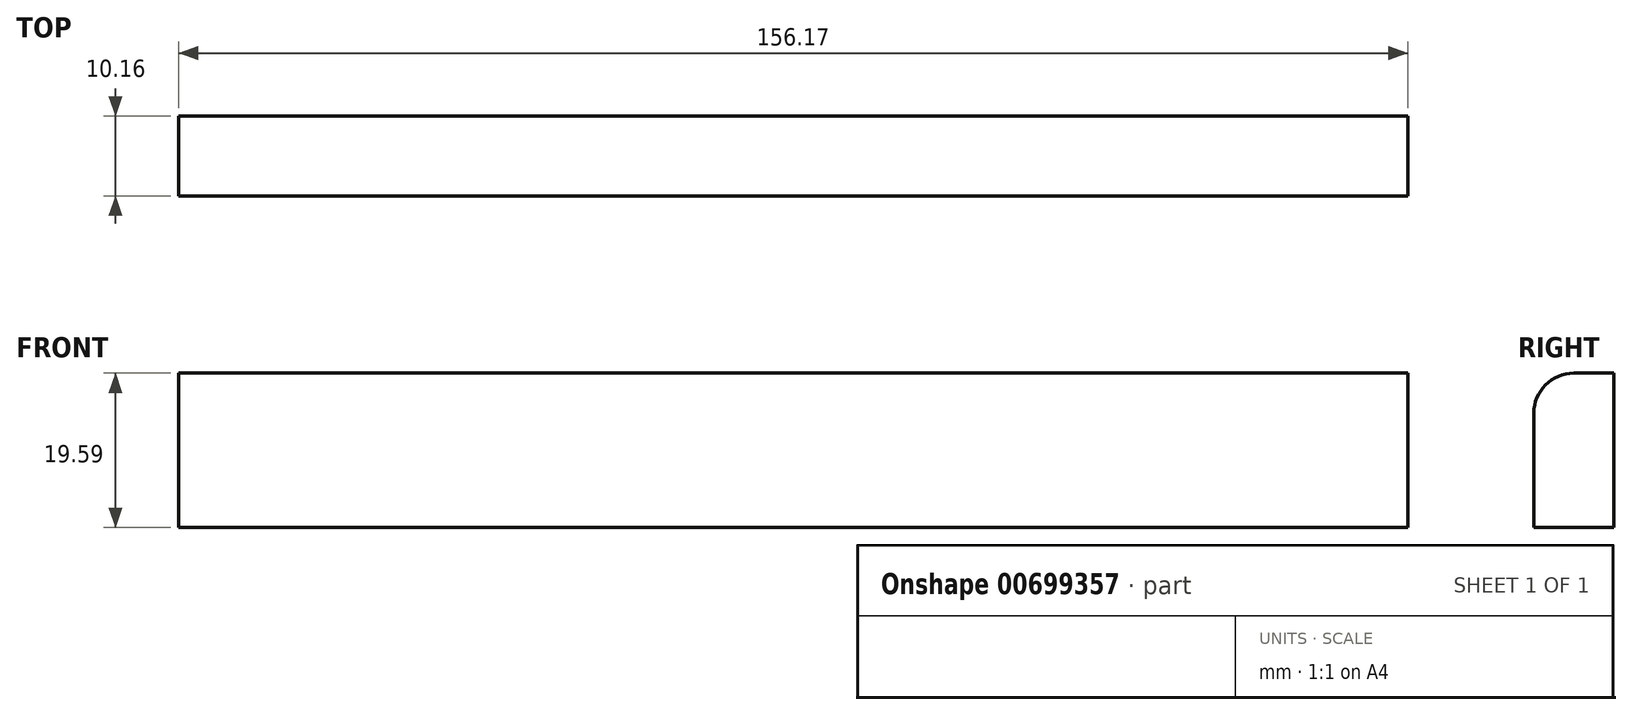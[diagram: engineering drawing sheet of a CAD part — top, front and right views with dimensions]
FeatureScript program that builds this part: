
annotation { "Feature Type Name" : "Feature", "Feature Type Description" : "" }
export const myFeature = defineFeature(function(context is Context, id is Id, definition is map)
    precondition{}
    {
        {
            var Q0;
            Q0=qCreatedBy(makeId("Front.planeOp"),FACE);
            var sketch = newSketch(context, id + "F0", { "sketchPlane" : qUnion([Q0])});
            skLineSegment(sketch, "E0", {"start": v(0, 0) * mm, "end": v(-78.6, 0) * mm});
            skLineSegment(sketch, "E1", {"start": v(-78.6, 0) * mm, "end": v(-78.6, -19.59) * mm});
            skLineSegment(sketch, "E2", {"start": v(-78.6, -19.59) * mm, "end": v(77.56, -19.59) * mm});
            skLineSegment(sketch, "E3", {"start": v(77.56, -19.59) * mm, "end": v(77.56, 0) * mm});
            skLineSegment(sketch, "E4", {"start": v(77.56, 0) * mm, "end": v(0, 0) * mm});
            skSolve(sketch);
        }
        {
            var Q0;
            Q0=makeQuery(id+"F0.imprint","IMPRINT",FACE,{"disambiguationData":[TD([[makeQuery(id+"F0.imprint","IMPRINT",EDGE,{"derivedFrom":sQuery(id+"F0.wireOp",EDGE,"E0")}),1.0]])]});
            extrude(context, id + "F1", {"entities" : qUnion([Q0]), "depth" : 10.16 * mm, "offsetDistance" : 25.4 * mm});
        }
        {
            var Q0;
            Q0=makeQuery(id+"F1.opExtrude","CAP_EDGE",EDGE,{"disambiguationData":[OSD([sQuery(id+"F0.wireOp",EDGE,"E0"),sQuery(id+"F0.wireOp",EDGE,"E4")])],"isStart":false});
            fillet(context, id + "F2", {"entities" : qUnion([Q0]), "radius" : 5.08 * mm, "tangentPropagation" : true, "allowEdgeOverflow" : false});
        }
    });
